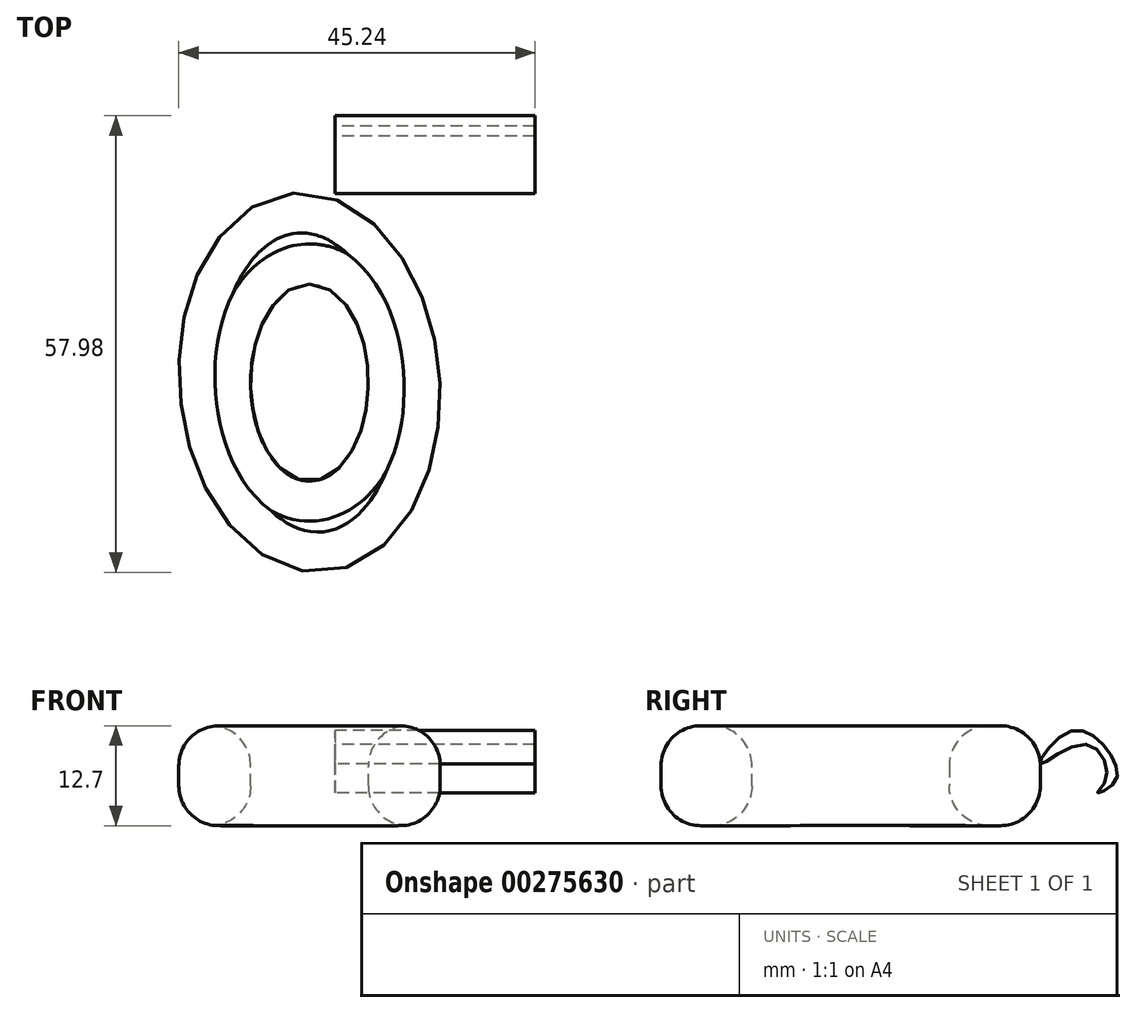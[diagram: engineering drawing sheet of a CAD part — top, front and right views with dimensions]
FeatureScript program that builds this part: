
annotation { "Feature Type Name" : "Feature", "Feature Type Description" : "" }
export const myFeature = defineFeature(function(context is Context, id is Id, definition is map)
    precondition{}
    {
        {
            var Q0;
            Q0=qCreatedBy(makeId("Top.planeOp"),FACE);
            var sketch = newSketch(context, id + "F0", { "sketchPlane" : qUnion([Q0])});
            skEllipse(sketch, "E0", {"center": v(-15.94, 11.89) * mm, "majorRadius": 24.14 * mm, "minorRadius": 16.54 * mm, "majorAxis": v(-0.08, 1)});
            skEllipse(sketch, "E1", {"center": v(-15.94, 11.89) * mm, "majorRadius": 12.53 * mm, "minorRadius": 7.48 * mm, "majorAxis": v(0, 1)});
            skSolve(sketch);
        }
        {
            var Q0;
            Q0=makeQuery(id+"F0.imprint","IMPRINT",FACE,{"disambiguationData":[TD([[makeQuery(id+"F0.imprint","IMPRINT",EDGE,{"derivedFrom":sQuery(id+"F0.wireOp",EDGE,"E0")}),1.0]])]});
            extrude(context, id + "F1", {"entities" : qUnion([Q0]), "depth" : 12.7 * mm});
        }
        {
            var Q0;
            Q0=makeQuery(id+"F1.opExtrude","CAP_EDGE",EDGE,{"disambiguationData":[OSD([sQuery(id+"F0.wireOp",EDGE,"E0")])],"isStart":false});
            var Q1;
            Q1=makeQuery(id+"F1.opExtrude","CAP_EDGE",EDGE,{"disambiguationData":[OSD([sQuery(id+"F0.wireOp",EDGE,"E1")])],"isStart":false});
            var Q2;
            Q2=makeQuery(id+"F1.opExtrude","CAP_EDGE",EDGE,{"disambiguationData":[OSD([sQuery(id+"F0.wireOp",EDGE,"E0")])],"isStart":true});
            var Q3;
            Q3=makeQuery(id+"F1.opExtrude","CAP_EDGE",EDGE,{"disambiguationData":[OSD([sQuery(id+"F0.wireOp",EDGE,"E1")])],"isStart":true});
            fillet(context, id + "F2", {"entities" : qUnion([Q0, Q1, Q2, Q3]), "radius" : 5.08 * mm, "tangentPropagation" : true, "allowEdgeOverflow" : false});
        }
        {
            var Q0;
            Q0=qCreatedBy(makeId("Right.planeOp"),FACE);
            var sketch = newSketch(context, id + "F3", { "sketchPlane" : qUnion([Q0])});
            skFitSpline(sketch, "E2", {"points": [v(35.96, 7.88) * mm, v(41.66, 10.34) * mm, v(44.35, 5.98) * mm, v(43.23, 4.2) * mm, v(45.47, 5.53) * mm, v(44.12, 10.12) * mm, v(39.32, 11.8) * mm, v(35.96, 7.88) * mm]});
            skSolve(sketch);
        }
        {
            var Q0;
            Q0 = qSketchRegion(id + "F3", true);
            extrude(context, id + "F4", {"entities" : qUnion([Q0]), "endBound" : BoundingType.SYMMETRIC, "depth" : 25.4 * mm});
        }
    });
